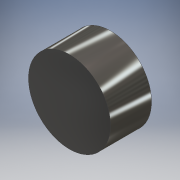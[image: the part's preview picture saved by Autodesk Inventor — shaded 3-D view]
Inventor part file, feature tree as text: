
AUTODESK INVENTOR PART (.ipt)
format: ipt  version: 2016 (Build 200138000, 138)  size: 94,208 bytes
history: native  units: mm
features: extrude x1, sketch x1
ambient origin geometry x8: Origin, YZ Plane, XZ Plane, XY Plane, X Axis, Y Axis, Z Axis, Center Point
bodies: Solid1 (feature_tree)
feature tree (2):
  extrude  "Extrusion1"  Depth=2.0mm TaperAngle=0.0deg
  sketch  "Sketch1"  dims[d0=4.0mm d1=2.0mm d2=0.0mm]
